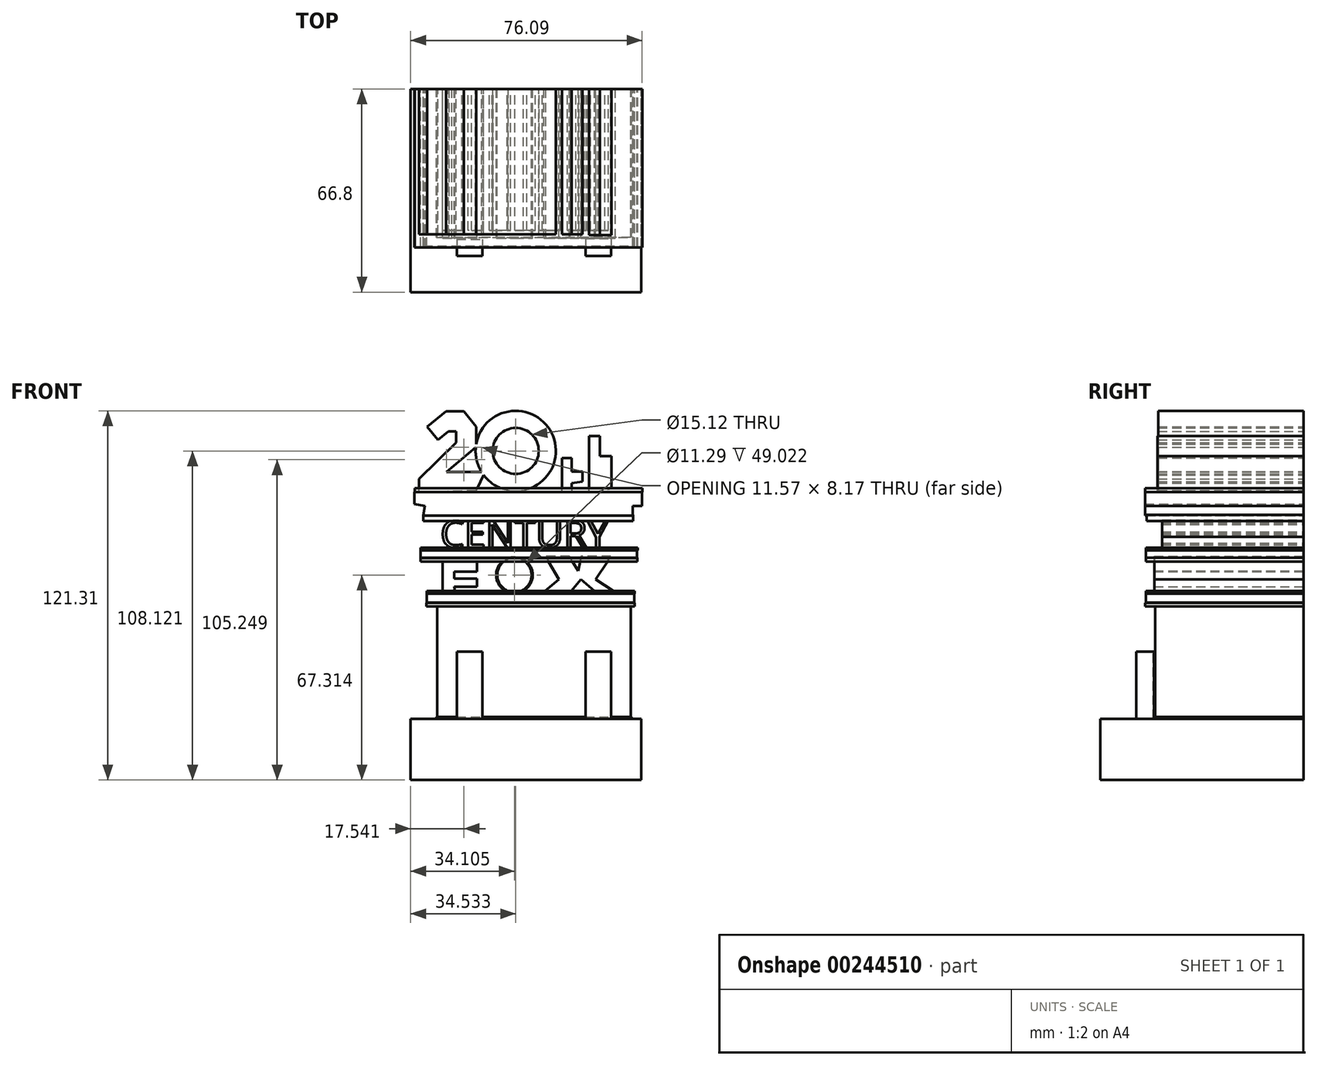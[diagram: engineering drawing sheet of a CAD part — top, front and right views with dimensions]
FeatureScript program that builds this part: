
annotation { "Feature Type Name" : "Feature", "Feature Type Description" : "" }
export const myFeature = defineFeature(function(context is Context, id is Id, definition is map)
    precondition{}
    {
        {
            var Q0;
            Q0=qCreatedBy(makeId("Front.planeOp"),FACE);
            var sketch = newSketch(context, id + "F0", { "sketchPlane" : qUnion([Q0])});
            skLineSegment(sketch, "E0.bottom", {"start": v(-27.1, -42.12) * mm, "end": v(48.68, -42.12) * mm});
            skLineSegment(sketch, "E0.top", {"start": v(-27.1, -22) * mm, "end": v(48.68, -22) * mm});
            skLineSegment(sketch, "E0.left", {"start": v(-27.1, -42.12) * mm, "end": v(-27.1, -22) * mm});
            skLineSegment(sketch, "E0.right", {"start": v(48.68, -42.12) * mm, "end": v(48.68, -22) * mm});
            skSolve(sketch);
        }
        {
            var Q0;
            Q0 = qSketchRegion(id + "F0", true);
            extrude(context, id + "F1", {"entities" : qUnion([Q0]), "depth" : 66.8 * mm});
        }
        {
            var Q0;
            Q0=qCreatedBy(makeId("Front.planeOp"),FACE);
            var sketch = newSketch(context, id + "F2", { "sketchPlane" : qUnion([Q0])});
            skLineSegment(sketch, "E1.bottom", {"start": v(-18.36, -21.44) * mm, "end": v(45.18, -21.44) * mm});
            skLineSegment(sketch, "E1.top", {"start": v(-18.36, 15.28) * mm, "end": v(45.18, 15.28) * mm});
            skLineSegment(sketch, "E1.left", {"start": v(-18.36, -21.44) * mm, "end": v(-18.36, 15.28) * mm});
            skLineSegment(sketch, "E1.right", {"start": v(45.18, -21.44) * mm, "end": v(45.18, 15.28) * mm});
            skSolve(sketch);
        }
        {
            var Q0;
            Q0 = qSketchRegion(id + "F2", true);
            extrude(context, id + "F3", {"entities" : qUnion([Q0]), "depth" : 48.77 * mm});
        }
        {
            var Q0;
            Q0=qCreatedBy(makeId("Top.planeOp"),FACE);
            var sketch = newSketch(context, id + "F4", { "sketchPlane" : qUnion([Q0])});
            skLineSegment(sketch, "E2.bottom", {"start": v(-11.95, -49.42) * mm, "end": v(-3.5, -49.42) * mm});
            skLineSegment(sketch, "E2.top", {"start": v(-11.95, -54.96) * mm, "end": v(-3.5, -54.96) * mm});
            skLineSegment(sketch, "E2.left", {"start": v(-11.95, -49.42) * mm, "end": v(-11.95, -54.96) * mm});
            skLineSegment(sketch, "E2.right", {"start": v(-3.5, -49.42) * mm, "end": v(-3.5, -54.96) * mm});
            skLineSegment(sketch, "E3.bottom", {"start": v(30.31, -49.13) * mm, "end": v(38.77, -49.13) * mm});
            skLineSegment(sketch, "E3.top", {"start": v(30.31, -54.96) * mm, "end": v(38.77, -54.96) * mm});
            skLineSegment(sketch, "E3.left", {"start": v(30.31, -49.13) * mm, "end": v(30.31, -54.96) * mm});
            skLineSegment(sketch, "E3.right", {"start": v(38.77, -49.13) * mm, "end": v(38.77, -54.96) * mm});
            skSolve(sketch);
        }
        {
            var Q0;
            Q0 = qSketchRegion(id + "F4", true);
            extrude(context, id + "F5", {"entities" : qUnion([Q0]), "operationType" : NewBodyOperationType.ADD, "oppositeDirection" : true, "depth" : 33.53 * mm});
        }
        {
            var Q0;
            Q0=qCreatedBy(makeId("Front.planeOp"),FACE);
            var sketch = newSketch(context, id + "F6", { "sketchPlane" : qUnion([Q0])});
            skLineSegment(sketch, "E4.bottom", {"start": v(-21.86, 16.16) * mm, "end": v(46.34, 16.16) * mm});
            skLineSegment(sketch, "E4.top", {"start": v(-21.86, 19.07) * mm, "end": v(46.34, 19.07) * mm});
            skLineSegment(sketch, "E4.left", {"start": v(-21.86, 16.16) * mm, "end": v(-21.86, 19.07) * mm});
            skLineSegment(sketch, "E4.right", {"start": v(46.34, 16.16) * mm, "end": v(46.34, 19.07) * mm});
            skSolve(sketch);
        }
        {
            var Q0;
            Q0 = qSketchRegion(id + "F6", true);
            extrude(context, id + "F7", {"entities" : qUnion([Q0]), "depth" : 51.82 * mm});
        }
        {
            var Q0;
            Q0=qCreatedBy(makeId("Front.planeOp"),FACE);
            var sketch = newSketch(context, id + "F8", { "sketchPlane" : qUnion([Q0])});
            skLineSegment(sketch, "E5", {"start": v(-16.61, 19.36) * mm, "end": v(-16.61, 29.86) * mm});
            skLineSegment(sketch, "E6", {"start": v(-16.61, 29.86) * mm, "end": v(-5.25, 29.86) * mm});
            skLineSegment(sketch, "E7", {"start": v(-5.25, 29.86) * mm, "end": v(-5.25, 26.36) * mm});
            skLineSegment(sketch, "E8", {"start": v(-5.25, 26.36) * mm, "end": v(-12.82, 26.36) * mm});
            skLineSegment(sketch, "E9", {"start": v(-12.82, 26.36) * mm, "end": v(-12.82, 24.03) * mm});
            skLineSegment(sketch, "E10", {"start": v(-12.82, 24.03) * mm, "end": v(-5.25, 24.03) * mm});
            skLineSegment(sketch, "E11", {"start": v(-5.25, 24.03) * mm, "end": v(-5.25, 21.4) * mm});
            skLineSegment(sketch, "E12", {"start": v(-5.25, 21.4) * mm, "end": v(-12.82, 21.4) * mm});
            skFitSpline(sketch, "E13", {"points": [v(-12.82, 21.4) * mm, v(-12.82, 19.36) * mm, v(-16.61, 19.36) * mm], "startDerivative": vector(1.4, -5.84) * mm, "endDerivative": vector(-8.46, 1.4) * mm});
            skCircle(sketch, "E14", {"center": v(7, 25.2) * mm, "radius": 6 * mm});
            skCircle(sketch, "E15", {"center": v(7, 25.2) * mm, "radius": 5.65 * mm});
            skLineSegment(sketch, "E16", {"start": v(17.3, 31.37) * mm, "end": v(21.57, 23.74) * mm});
            skLineSegment(sketch, "E17", {"start": v(16.6, 19.55) * mm, "end": v(25.26, 19.55) * mm});
            skLineSegment(sketch, "E18", {"start": v(25.26, 19.55) * mm, "end": v(28.86, 23.74) * mm});
            skLineSegment(sketch, "E19", {"start": v(28.86, 23.74) * mm, "end": v(33.73, 19.55) * mm});
            skLineSegment(sketch, "E20", {"start": v(33.73, 19.55) * mm, "end": v(40.19, 19.55) * mm});
            skLineSegment(sketch, "E21", {"start": v(40.19, 19.55) * mm, "end": v(33.73, 23.74) * mm});
            skLineSegment(sketch, "E22", {"start": v(33.73, 23.74) * mm, "end": v(38.68, 31.37) * mm});
            skLineSegment(sketch, "E23", {"start": v(38.68, 31.37) * mm, "end": v(28.86, 31.37) * mm});
            skLineSegment(sketch, "E24", {"start": v(27.99, 26.55) * mm, "end": v(25.07, 31.37) * mm});
            skLineSegment(sketch, "E25", {"start": v(25.07, 31.37) * mm, "end": v(17.3, 31.37) * mm});
            skLineSegment(sketch, "E26", {"start": v(28.86, 31.37) * mm, "end": v(27.99, 26.55) * mm});
            skLineSegment(sketch, "E27", {"start": v(21.57, 23.74) * mm, "end": v(16.6, 19.55) * mm});
            skSolve(sketch);
        }
        {
            var Q0;
            Q0 = qSketchRegion(id + "F8", true);
            extrude(context, id + "F9", {"entities" : qUnion([Q0]), "operationType" : NewBodyOperationType.ADD, "depth" : 49.02 * mm});
        }
        {
            var Q0;
            Q0=qCreatedBy(makeId("Front.planeOp"),FACE);
            var sketch = newSketch(context, id + "F10", { "sketchPlane" : qUnion([Q0])});
            skLineSegment(sketch, "E28.bottom", {"start": v(-23.9, 33.37) * mm, "end": v(47.22, 33.37) * mm});
            skLineSegment(sketch, "E28.top", {"start": v(-23.9, 30.75) * mm, "end": v(47.22, 30.75) * mm});
            skLineSegment(sketch, "E28.left", {"start": v(-23.9, 33.37) * mm, "end": v(-23.9, 30.75) * mm});
            skLineSegment(sketch, "E28.right", {"start": v(47.22, 33.37) * mm, "end": v(47.22, 30.75) * mm});
            skSolve(sketch);
        }
        {
            var Q0;
            Q0 = qSketchRegion(id + "F10", true);
            extrude(context, id + "F11", {"entities" : qUnion([Q0]), "depth" : 51.82 * mm});
        }
        {
            var Q0;
            Q0=qCreatedBy(makeId("Front.planeOp"),FACE);
            var sketch = newSketch(context, id + "F12", { "sketchPlane" : qUnion([Q0])});
            skText(sketch, "E29", { "text": "CENTURY", "fontName": "OpenSans-Regular.ttf"});
            const initialGuessF12  = {"E29": [-0.01734, 0.03424, 1, 0, 0.00904]};
            skSetInitialGuess(sketch, initialGuessF12);
            skSolve(sketch);
        }
        {
            var Q0;
            Q0 = qSketchRegion(id + "F12", true);
            extrude(context, id + "F13", {"entities" : qUnion([Q0]), "depth" : 46.48 * mm});
        }
        {
            var Q0;
            Q0=qCreatedBy(makeId("Front.planeOp"),FACE);
            var sketch = newSketch(context, id + "F14", { "sketchPlane" : qUnion([Q0])});
            skLineSegment(sketch, "E30", {"start": v(-22.98, 44.79) * mm, "end": v(45.82, 44.79) * mm});
            skLineSegment(sketch, "E31", {"start": v(45.82, 44.79) * mm, "end": v(45.82, 47.93) * mm});
            skLineSegment(sketch, "E32", {"start": v(45.82, 47.93) * mm, "end": v(-22.41, 47.93) * mm});
            skLineSegment(sketch, "E33", {"start": v(-22.41, 47.93) * mm, "end": v(-22.98, 44.79) * mm});
            skLineSegment(sketch, "E34", {"start": v(-22.41, 47.93) * mm, "end": v(-25.88, 48.56) * mm});
            skLineSegment(sketch, "E35", {"start": v(-25.88, 48.56) * mm, "end": v(-25.88, 52.5) * mm});
            skLineSegment(sketch, "E36", {"start": v(-25.88, 52.5) * mm, "end": v(5.85, 52.5) * mm});
            skLineSegment(sketch, "E37", {"start": v(5.85, 52.5) * mm, "end": v(24.12, 52.5) * mm});
            skLineSegment(sketch, "E38", {"start": v(24.12, 52.5) * mm, "end": v(48.96, 52.5) * mm});
            skLineSegment(sketch, "E39", {"start": v(48.96, 52.5) * mm, "end": v(48.96, 47.93) * mm});
            skLineSegment(sketch, "E40", {"start": v(48.96, 47.93) * mm, "end": v(45.82, 47.93) * mm});
            skSolve(sketch);
        }
        {
            var Q0;
            Q0 = qSketchRegion(id + "F14", true);
            extrude(context, id + "F15", {"entities" : qUnion([Q0]), "depth" : 52.07 * mm});
        }
        {
            var Q0;
            Q0=qCreatedBy(makeId("Front.planeOp"),FACE);
            var sketch = newSketch(context, id + "F16", { "sketchPlane" : qUnion([Q0])});
            skLineSegment(sketch, "E41", {"start": v(-24.41, 52.5) * mm, "end": v(-24.41, 56.78) * mm});
            skLineSegment(sketch, "E42", {"start": v(-24.41, 56.78) * mm, "end": v(-12.13, 68.77) * mm});
            skLineSegment(sketch, "E43", {"start": v(-12.13, 68.77) * mm, "end": v(-12.13, 72.48) * mm});
            skLineSegment(sketch, "E44", {"start": v(-12.13, 72.48) * mm, "end": v(-14.7, 72.48) * mm});
            skLineSegment(sketch, "E45", {"start": v(-14.7, 72.48) * mm, "end": v(-18.13, 69.63) * mm});
            skLineSegment(sketch, "E46", {"start": v(-18.13, 69.63) * mm, "end": v(-21.69, 73.9) * mm});
            skLineSegment(sketch, "E47", {"start": v(-21.69, 73.9) * mm, "end": v(-15.5, 79.04) * mm});
            skLineSegment(sketch, "E48", {"start": v(-15.5, 79.04) * mm, "end": v(-9.57, 79.04) * mm});
            skLineSegment(sketch, "E49", {"start": v(-9.57, 79.04) * mm, "end": v(-5.57, 73.9) * mm});
            skLineSegment(sketch, "E50", {"start": v(-5.57, 73.9) * mm, "end": v(-5.57, 67.33) * mm});
            skLineSegment(sketch, "E51", {"start": v(-5.57, 67.33) * mm, "end": v(-15.36, 59.05) * mm});
            skLineSegment(sketch, "E52", {"start": v(-15.36, 59.05) * mm, "end": v(-2.72, 59.05) * mm});
            skLineSegment(sketch, "E53", {"start": v(-2.72, 59.05) * mm, "end": v(-5.64, 52.94) * mm});
            skLineSegment(sketch, "E54", {"start": v(-5.64, 52.94) * mm, "end": v(-24.41, 52.5) * mm});
            skCircle(sketch, "E55", {"center": v(7.42, 66) * mm, "radius": 13.19 * mm});
            skCircle(sketch, "E56", {"center": v(7.42, 66) * mm, "radius": 7.56 * mm});
            skLineSegment(sketch, "E57", {"start": v(22.57, 51.75) * mm, "end": v(22.57, 63.63) * mm});
            skLineSegment(sketch, "E58", {"start": v(22.57, 63.63) * mm, "end": v(25.83, 63.63) * mm});
            skLineSegment(sketch, "E59", {"start": v(25.83, 63.63) * mm, "end": v(25.83, 59.17) * mm});
            skLineSegment(sketch, "E60", {"start": v(25.53, 59.17) * mm, "end": v(29.4, 59.17) * mm});
            skLineSegment(sketch, "E61", {"start": v(29.4, 59.17) * mm, "end": v(29.4, 55.9) * mm});
            skLineSegment(sketch, "E62", {"start": v(29.4, 55.9) * mm, "end": v(25.83, 55.38) * mm});
            skLineSegment(sketch, "E63", {"start": v(25.83, 55.38) * mm, "end": v(25.83, 51.75) * mm});
            skLineSegment(sketch, "E64", {"start": v(25.83, 51.75) * mm, "end": v(22.57, 51.75) * mm});
            skLineSegment(sketch, "E65", {"start": v(34.44, 51.75) * mm, "end": v(34.44, 70.45) * mm});
            skLineSegment(sketch, "E66", {"start": v(34.44, 70.45) * mm, "end": v(37.43, 71.87) * mm});
            skLineSegment(sketch, "E67", {"start": v(37.43, 71.87) * mm, "end": v(37.43, 63.63) * mm});
            skLineSegment(sketch, "E68", {"start": v(37.43, 63.63) * mm, "end": v(37.43, 63.63) * mm});
            skLineSegment(sketch, "E69", {"start": v(37.43, 63.63) * mm, "end": v(43.94, 63.63) * mm});
            skLineSegment(sketch, "E70", {"start": v(43.94, 63.63) * mm, "end": v(43.94, 52.62) * mm});
            skLineSegment(sketch, "E71", {"start": v(40.38, 52.62) * mm, "end": v(40.38, 58.13) * mm});
            skPoint(sketch, "E71.endSnap0", {"position": v(43.94, 58.13) * mm});
            skLineSegment(sketch, "E72", {"start": v(40.38, 58.13) * mm, "end": v(37.43, 58.13) * mm});
            skLineSegment(sketch, "E73", {"start": v(37.43, 58.13) * mm, "end": v(37.43, 52.62) * mm});
            skLineSegment(sketch, "E74", {"start": v(37.43, 52.62) * mm, "end": v(34.44, 51.75) * mm});
            skSolve(sketch);
        }
        {
            var Q0;
            Q0 = qSketchRegion(id + "F16", true);
            extrude(context, id + "F17", {"entities" : qUnion([Q0]), "operationType" : NewBodyOperationType.ADD, "depth" : 47.75 * mm});
        }
        {
            var Q0;
            Q0=qCreatedBy(makeId("Front.planeOp"),FACE);
            var sketch = newSketch(context, id + "F18", { "sketchPlane" : qUnion([Q0])});
            skLineSegment(sketch, "E75", {"start": v(31.5, 52.17) * mm, "end": v(31.5, 70.89) * mm});
            skLineSegment(sketch, "E76", {"start": v(35.07, 70.89) * mm, "end": v(35.07, 64.35) * mm});
            skLineSegment(sketch, "E77", {"start": v(35.07, 64.35) * mm, "end": v(38.93, 64.35) * mm});
            skLineSegment(sketch, "E78", {"start": v(38.93, 64.35) * mm, "end": v(38.93, 53.65) * mm});
            skLineSegment(sketch, "E79", {"start": v(36.26, 53.65) * mm, "end": v(36.26, 59) * mm});
            skPoint(sketch, "E79.endSnap0", {"position": v(38.93, 59) * mm});
            skLineSegment(sketch, "E80", {"start": v(31.5, 70.89) * mm, "end": v(35.07, 70.89) * mm});
            skLineSegment(sketch, "E81", {"start": v(31.5, 52.17) * mm, "end": v(38.93, 53.65) * mm});
            skSolve(sketch);
        }
        {
            var Q0;
            Q0 = qSketchRegion(id + "F18", true);
            extrude(context, id + "F19", {"entities" : qUnion([Q0]), "operationType" : NewBodyOperationType.ADD, "depth" : 48 * mm});
        }
        {
            var Q0;
            Q0=qCreatedBy(makeId("Front.planeOp"),FACE);
            var sketch = newSketch(context, id + "F20", { "sketchPlane" : qUnion([Q0])});
            skLineSegment(sketch, "E82.bottom", {"start": v(-22.9, 45.04) * mm, "end": v(46.02, 45.04) * mm});
            skLineSegment(sketch, "E82.top", {"start": v(-22.9, 43) * mm, "end": v(46.02, 43) * mm});
            skLineSegment(sketch, "E82.left", {"start": v(-22.9, 45.04) * mm, "end": v(-22.9, 43) * mm});
            skLineSegment(sketch, "E82.right", {"start": v(46.02, 45.04) * mm, "end": v(46.02, 43) * mm});
            skSolve(sketch);
        }
        {
            var Q0;
            Q0 = qSketchRegion(id + "F20", true);
            extrude(context, id + "F21", {"entities" : qUnion([Q0]), "depth" : 51.56 * mm});
        }
        {
            var Q0;
            Q0=qCreatedBy(makeId("Front.planeOp"),FACE);
            var sketch = newSketch(context, id + "F22", { "sketchPlane" : qUnion([Q0])});
            skLineSegment(sketch, "E83.bottom", {"start": v(-23.82, 33.31) * mm, "end": v(47.51, 33.31) * mm});
            skLineSegment(sketch, "E83.top", {"start": v(-23.82, 34.21) * mm, "end": v(47.51, 34.21) * mm});
            skLineSegment(sketch, "E83.left", {"start": v(-23.82, 33.31) * mm, "end": v(-23.82, 34.21) * mm});
            skLineSegment(sketch, "E83.right", {"start": v(47.51, 33.31) * mm, "end": v(47.51, 34.21) * mm});
            skSolve(sketch);
        }
        {
            var Q0;
            Q0 = qSketchRegion(id + "F22", true);
            extrude(context, id + "F23", {"entities" : qUnion([Q0]), "depth" : 51.82 * mm});
        }
        {
            var Q0;
            Q0=qCreatedBy(makeId("Front.planeOp"),FACE);
            var sketch = newSketch(context, id + "F24", { "sketchPlane" : qUnion([Q0])});
            skLineSegment(sketch, "E84.bottom", {"start": v(-21.96, 16.03) * mm, "end": v(46.5, 16.03) * mm});
            skLineSegment(sketch, "E84.top", {"start": v(-21.96, 14.84) * mm, "end": v(46.5, 14.84) * mm});
            skLineSegment(sketch, "E84.left", {"start": v(-21.96, 16.03) * mm, "end": v(-21.96, 14.84) * mm});
            skLineSegment(sketch, "E84.right", {"start": v(46.5, 16.03) * mm, "end": v(46.5, 14.84) * mm});
            skSolve(sketch);
        }
        {
            var Q0;
            Q0 = qSketchRegion(id + "F24", true);
            extrude(context, id + "F25", {"entities" : qUnion([Q0]), "operationType" : NewBodyOperationType.ADD, "depth" : 52.07 * mm});
        }
        {
            var Q0;
            Q0=qCreatedBy(makeId("Front.planeOp"),FACE);
            var sketch = newSketch(context, id + "F26", { "sketchPlane" : qUnion([Q0])});
            skLineSegment(sketch, "E85.bottom", {"start": v(-23.92, 30.88) * mm, "end": v(47.44, 30.88) * mm});
            skLineSegment(sketch, "E85.top", {"start": v(-23.92, 29.68) * mm, "end": v(47.44, 29.68) * mm});
            skLineSegment(sketch, "E85.left", {"start": v(-23.92, 30.88) * mm, "end": v(-23.92, 29.68) * mm});
            skLineSegment(sketch, "E85.right", {"start": v(47.44, 30.88) * mm, "end": v(47.44, 29.68) * mm});
            skSolve(sketch);
        }
        {
            var Q0;
            Q0 = qSketchRegion(id + "F26", true);
            extrude(context, id + "F27", {"entities" : qUnion([Q0]), "depth" : 51.82 * mm});
        }
        {
            var Q0;
            Q0=qCreatedBy(makeId("Front.planeOp"),FACE);
            var sketch = newSketch(context, id + "F28", { "sketchPlane" : qUnion([Q0])});
            skLineSegment(sketch, "E86.bottom", {"start": v(-21.88, 19.13) * mm, "end": v(46.48, 19.13) * mm});
            skLineSegment(sketch, "E86.top", {"start": v(-21.88, 19.97) * mm, "end": v(46.48, 19.97) * mm});
            skLineSegment(sketch, "E86.left", {"start": v(-21.88, 19.13) * mm, "end": v(-21.88, 19.97) * mm});
            skLineSegment(sketch, "E86.right", {"start": v(46.48, 19.13) * mm, "end": v(46.48, 19.97) * mm});
            skSolve(sketch);
        }
        {
            var Q0;
            Q0 = qSketchRegion(id + "F28", true);
            extrude(context, id + "F29", {"entities" : qUnion([Q0]), "depth" : 51.82 * mm});
        }
        {
            var Q0;
            Q0=qCreatedBy(makeId("Front.planeOp"),FACE);
            var sketch = newSketch(context, id + "F30", { "sketchPlane" : qUnion([Q0])});
            skLineSegment(sketch, "E87.bottom", {"start": v(-18.59, -22.01) * mm, "end": v(45.44, -22.01) * mm});
            skLineSegment(sketch, "E87.top", {"start": v(-18.59, -21.4) * mm, "end": v(45.44, -21.4) * mm});
            skLineSegment(sketch, "E87.left", {"start": v(-18.59, -22.01) * mm, "end": v(-18.59, -21.4) * mm});
            skLineSegment(sketch, "E87.right", {"start": v(45.44, -22.01) * mm, "end": v(45.44, -21.4) * mm});
            skSolve(sketch);
        }
        {
            var Q0;
            Q0 = qSketchRegion(id + "F30", true);
            extrude(context, id + "F31", {"entities" : qUnion([Q0]), "depth" : 48.77 * mm});
        }
        {
            var Q0;
            Q0=qCreatedBy(makeId("Front.planeOp"),FACE);
            var sketch = newSketch(context, id + "F32", { "sketchPlane" : qUnion([Q0])});
            skLineSegment(sketch, "E88.bottom", {"start": v(-25.8, 52.45) * mm, "end": v(48.98, 52.45) * mm});
            skLineSegment(sketch, "E88.top", {"start": v(-25.8, 53.78) * mm, "end": v(48.98, 53.78) * mm});
            skLineSegment(sketch, "E88.left", {"start": v(-25.8, 52.45) * mm, "end": v(-25.8, 53.78) * mm});
            skLineSegment(sketch, "E88.right", {"start": v(48.98, 52.45) * mm, "end": v(48.98, 53.78) * mm});
            skSolve(sketch);
        }
        {
            var Q0;
            Q0 = qSketchRegion(id + "F32", true);
            extrude(context, id + "F33", {"entities" : qUnion([Q0]), "depth" : 52.07 * mm});
        }
    });
